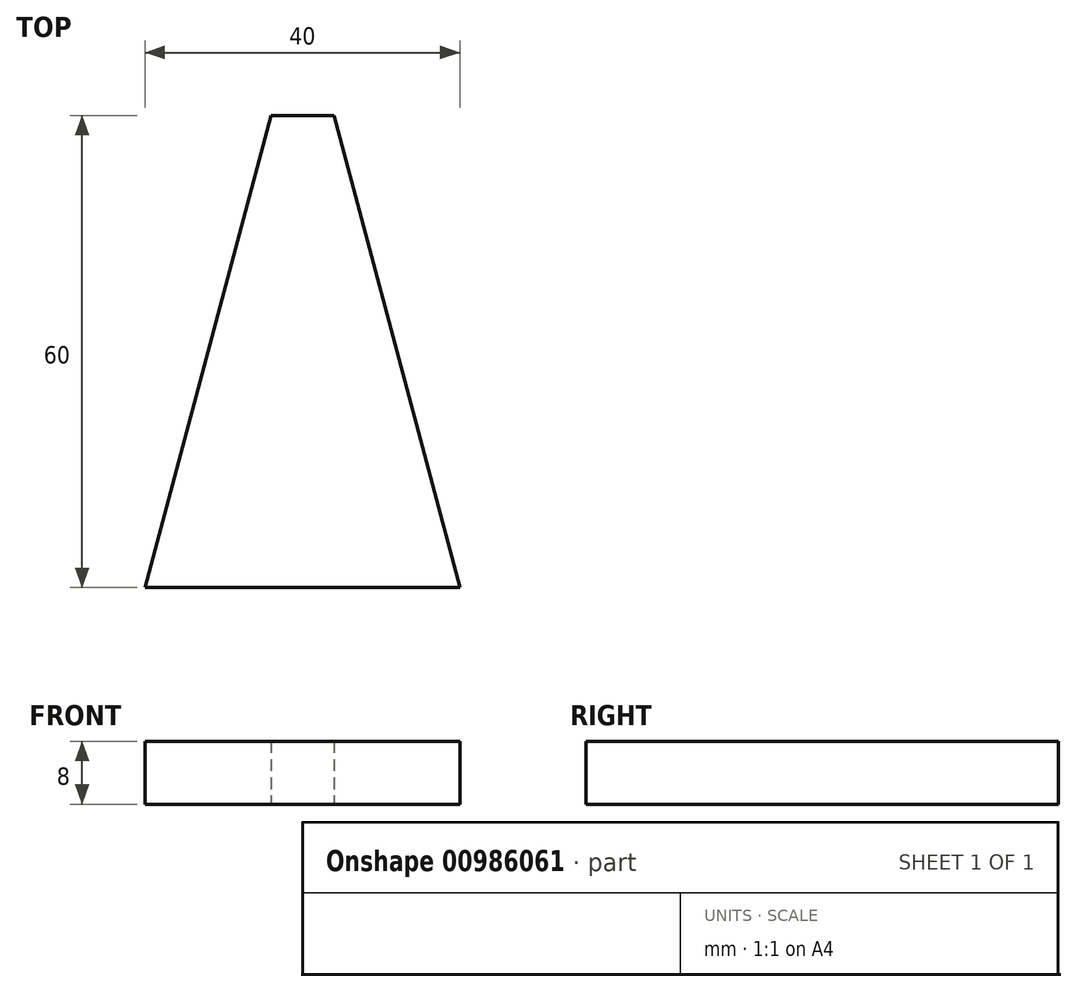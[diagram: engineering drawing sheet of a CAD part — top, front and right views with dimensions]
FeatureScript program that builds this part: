
annotation { "Feature Type Name" : "Feature", "Feature Type Description" : "" }
export const myFeature = defineFeature(function(context is Context, id is Id, definition is map)
    precondition{}
    {
        {
            var Q0;
            Q0=qCreatedBy(makeId("Top.planeOp"),FACE);
            var sketch = newSketch(context, id + "F0", { "sketchPlane" : qUnion([Q0])});
            skLineSegment(sketch, "E0", {"start": v(0, 0) * mm, "end": v(0, 60) * mm});
            skLineSegment(sketch, "E1", {"start": v(0, 60) * mm, "end": v(-4, 60) * mm});
            skLineSegment(sketch, "E2", {"start": v(-4, 60) * mm, "end": v(-20, 0) * mm});
            skLineSegment(sketch, "E3", {"start": v(-20, 0) * mm, "end": v(0, 0) * mm});
            skLineSegment(sketch, "E4.MirrorCS", {"start": v(20, 0) * mm, "end": v(0, 0) * mm});
            skLineSegment(sketch, "E5.MirrorCS", {"start": v(4, 60) * mm, "end": v(20, 0) * mm});
            skLineSegment(sketch, "E6.MirrorCS", {"start": v(0, 60) * mm, "end": v(4, 60) * mm});
            skSolve(sketch);
        }
        {
            var Q0;
            Q0=makeQuery(id+"F0.imprint","IMPRINT",FACE,{"disambiguationData":[TD([[makeQuery(id+"F0.imprint","IMPRINT",EDGE,{"derivedFrom":sQuery(id+"F0.wireOp",EDGE,"E0")}),1.0]])]});
            var Q1;
            Q1=makeQuery(id+"F0.imprint","IMPRINT",FACE,{"disambiguationData":[TD([[makeQuery(id+"F0.imprint","IMPRINT",EDGE,{"derivedFrom":sQuery(id+"F0.wireOp",EDGE,"E0")}),-1.0]])]});
            extrude(context, id + "F1", {"entities" : qUnion([Q0, Q1]), "depth" : 8 * mm, "offsetDistance" : 25 * mm});
        }
    });
